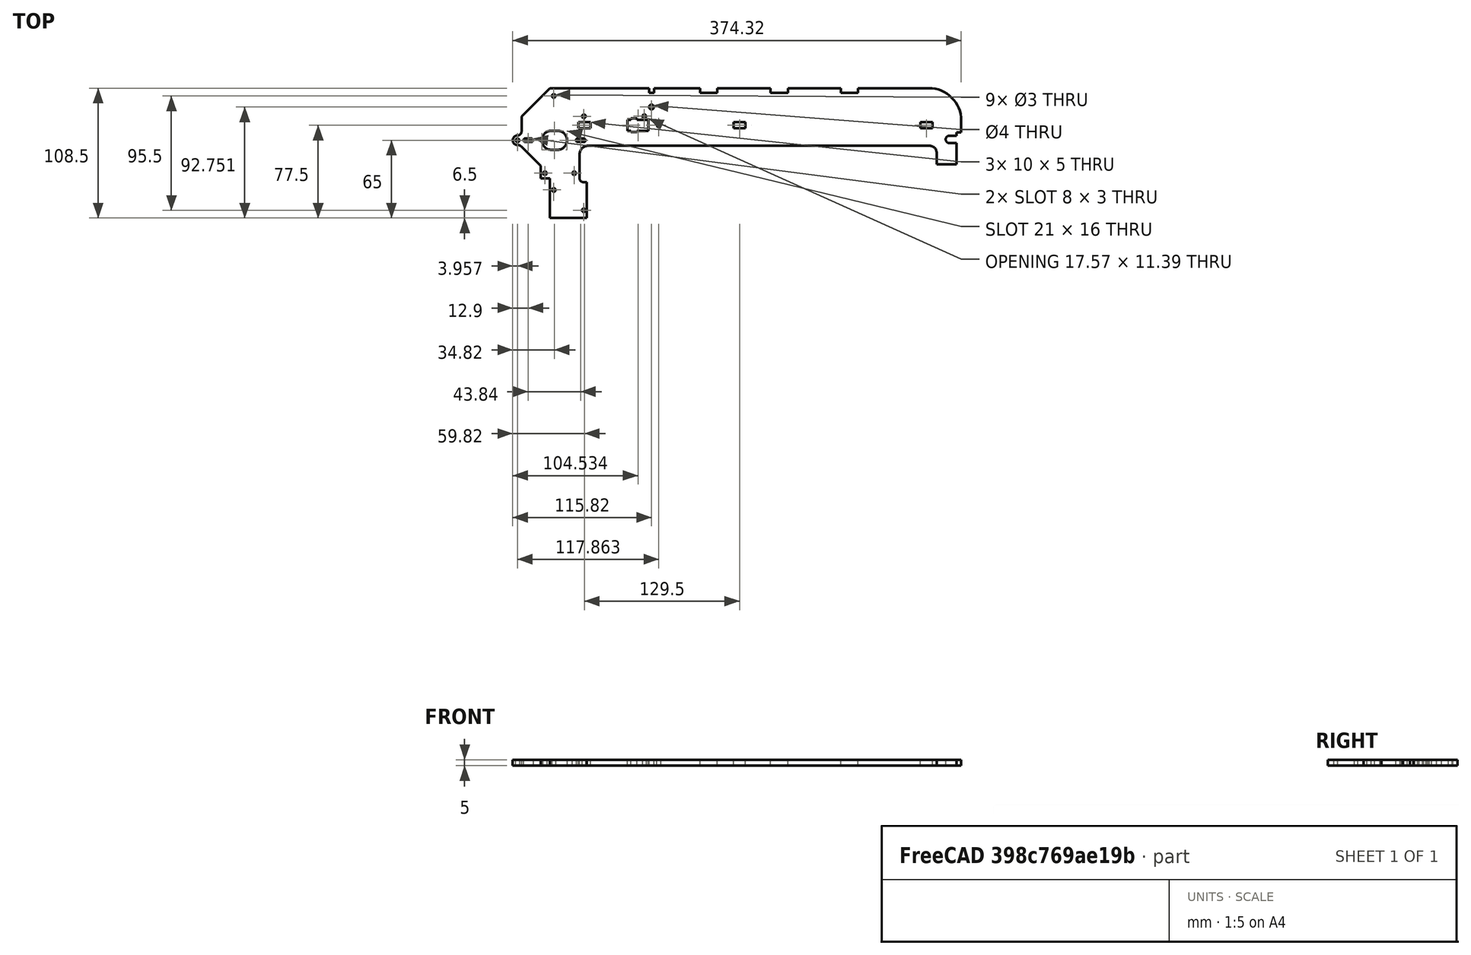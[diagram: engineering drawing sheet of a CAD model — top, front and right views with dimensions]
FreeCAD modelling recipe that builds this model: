
FCSTD DOCUMENT  (FreeCAD 0.17R13541 (Git))
Label: xx_561_x-axis-plate
License: All rights reserved
LicenseURL: http://en.wikipedia.org/wiki/All_rights_reserved
objects: Sketcher::SketchObject×1, PartDesign::Pad×1, PartDesign::Body×1
note: 4 computed .brp shape members not serialized (recipe doc carries the construction recipe); baked Part::Feature solids carry a one-line shape summary decoded from their .brp

FEATURE [Sketcher::SketchObject] Sketch090
  MapMode = 5
  Support = -> [XY_Plane]
  sketch-geometry (90):
    g0: Circle CenterX=78.5 CenterY=27.7514 CenterZ=0 NormalX=0 NormalY=0 NormalZ=-1 AngleXU=0 Radius=2
    g1: LineSegment StartX=66.4277 StartY=17 StartZ=0 EndX=66.4277 EndY=18.1939 EndZ=0
    g2: LineSegment StartX=24.5 StartY=-35 StartZ=0 EndX=21.5 EndY=-35 EndZ=0
    g3: LineSegment StartX=133.5 StartY=39.5 StartZ=0 EndX=119 EndY=39.5 EndZ=0
    g4: ArcOfCircle CenterX=21.92 CenterY=-1.78646e-06 CenterZ=0 NormalX=0 NormalY=0 NormalZ=1 AngleXU=0 Radius=1.5 StartAngle=4.7126 EndAngle=7.85377
    g5: LineSegment StartX=61.4277 StartY=6.8061 StartZ=0 EndX=66.4277 EndY=6.8061 EndZ=0
    g6: LineSegment StartX=-21.9203 StartY=1.5 StartZ=0 EndX=-26.9203 EndY=1.5 EndZ=0
    g7: ArcOfCircle CenterX=310 CenterY=16.5 CenterZ=0 NormalX=0 NormalY=0 NormalZ=1 AngleXU=0 Radius=27 StartAngle=0 EndAngle=1.5708
    g8: LineSegment StartX=333 StartY=-20 StartZ=0 EndX=333 EndY=-2.3 EndZ=0
    g9: LineSegment StartX=58.4277 StartY=17 StartZ=0 EndX=58.4277 EndY=8 EndZ=0
    g10: LineSegment StartX=-14 StartY=-21.3553 StartZ=0 EndX=-14 EndY=-32 EndZ=0
    g11: LineSegment StartX=25.5 StartY=-4.6 StartZ=0 EndX=310.5 EndY=-4.6 EndZ=0
    g12: Circle CenterX=-3.05 CenterY=-41.5 CenterZ=0 NormalX=0 NormalY=0 NormalZ=-1 AngleXU=0 Radius=1.5
    g13: Circle CenterX=84.5 CenterY=12.5 CenterZ=0 NormalX=0 NormalY=0 NormalZ=-1 AngleXU=0 Radius=1.5
    g14: LineSegment StartX=66.4277 StartY=18.1939 StartZ=0 EndX=61.4277 EndY=18.1939 EndZ=0
    g15: ArcOfCircle CenterX=-26.9203 CenterY=0 CenterZ=0 NormalX=0 NormalY=0 NormalZ=1 AngleXU=0 Radius=1.5 StartAngle=1.5708 EndAngle=4.71239
    g16: LineSegment StartX=80.5 StartY=43.5 StartZ=0 EndX=80.5 EndY=39.5 EndZ=0
    g17: LineSegment StartX=157 StartY=10 StartZ=0 EndX=157 EndY=15 EndZ=0
    g18: LineSegment StartX=61.4277 StartY=8 StartZ=0 EndX=61.4277 EndY=6.8061 EndZ=0
    g19: LineSegment StartX=313 StartY=10 StartZ=0 EndX=313 EndY=15 EndZ=0
    g20: Circle CenterX=22.05 CenterY=-58.5 CenterZ=0 NormalX=0 NormalY=0 NormalZ=-1 AngleXU=0 Radius=1.5
    g21: Circle CenterX=72.5 CenterY=20.1 CenterZ=0 NormalX=0 NormalY=0 NormalZ=-1 AngleXU=0 Radius=1.5
    g22: LineSegment StartX=-5 StartY=-8 StartZ=0 EndX=0 EndY=-8 EndZ=0
    g23: ArcOfCircle CenterX=-33.36 CenterY=0 CenterZ=0 NormalX=0 NormalY=0 NormalZ=1 AngleXU=0 Radius=3.96229 StartAngle=1.57159 EndAngle=4.7116
    g24: LineSegment StartX=76 StartY=8 StartZ=0 EndX=76 EndY=17 EndZ=0
    g25: LineSegment StartX=333 StartY=6.7 StartZ=0 EndX=337 EndY=6.7 EndZ=0
    g26: ArcOfCircle CenterX=-21.92 CenterY=0 CenterZ=0 NormalX=0 NormalY=0 NormalZ=1 AngleXU=0 Radius=1.5 StartAngle=4.71218 EndAngle=7.85419
    g27: LineSegment StartX=316.5 StartY=-10.6 StartZ=0 EndX=316.5 EndY=-20 EndZ=0
    g28: LineSegment StartX=303 StartY=10 StartZ=0 EndX=313 EndY=10 EndZ=0
    g29: LineSegment StartX=337 StartY=6.7 StartZ=0 EndX=337 EndY=16.5 EndZ=0
    g30: LineSegment StartX=313 StartY=15 StartZ=0 EndX=303 EndY=15 EndZ=0
    g31: LineSegment StartX=147 StartY=15 StartZ=0 EndX=147 EndY=10 EndZ=0
    g32: LineSegment StartX=-14 StartY=-32 StartZ=0 EndX=-6.5 EndY=-32 EndZ=0
    g33: LineSegment StartX=76.5 StartY=43.5 StartZ=0 EndX=-6.5 EndY=43.5 EndZ=0
    g34: LineSegment StartX=327 StartY=3.7 StartZ=0 EndX=333 EndY=3.7 EndZ=0
    g35: ArcOfCircle CenterX=-33.3631 CenterY=7.32541 CenterZ=0 NormalX=0 NormalY=0 NormalZ=1 AngleXU=0 Radius=3.36313 StartAngle=4.71239 EndAngle=6.28319
    g36: LineSegment StartX=-30 StartY=20 StartZ=0 EndX=-30 EndY=7.32541 EndZ=0
    g37: LineSegment StartX=177.75 StartY=43.5 StartZ=0 EndX=133.5 EndY=43.5 EndZ=0
    g38: LineSegment StartX=18.5 StartY=-32 StartZ=0 EndX=18.5 EndY=-11.6 EndZ=0
    g39: LineSegment StartX=-6.5 StartY=-32 StartZ=0 EndX=-6.5 EndY=-65 EndZ=0
    g40: LineSegment StartX=61.4277 StartY=18.1939 StartZ=0 EndX=61.4277 EndY=17 EndZ=0
    g41: Circle CenterX=-33.3631 CenterY=0 CenterZ=0 NormalX=0 NormalY=0 NormalZ=-1 AngleXU=0 Radius=1.5
    g42: LineSegment StartX=0 StartY=8 StartZ=0 EndX=-5 EndY=8 EndZ=0
    g43: LineSegment StartX=27.5 StartY=15 StartZ=0 EndX=17.5 EndY=15 EndZ=0
    g44: LineSegment StartX=316.5 StartY=-20 StartZ=0 EndX=333 EndY=-20 EndZ=0
    g45: LineSegment StartX=192.25 StartY=39.5 StartZ=0 EndX=177.75 EndY=39.5 EndZ=0
    g46: Circle CenterX=-10.5 CenterY=-27.55 CenterZ=0 NormalX=0 NormalY=0 NormalZ=-1 AngleXU=0 Radius=1.5
    g47: LineSegment StartX=119 StartY=43.5 StartZ=0 EndX=80.5 EndY=43.5 EndZ=0
    g48: ArcOfCircle CenterX=-5 CenterY=0 CenterZ=0 NormalX=0 NormalY=0 NormalZ=1 AngleXU=0 Radius=8 StartAngle=1.5708 EndAngle=4.71239
    g49: ArcOfCircle CenterX=310.5 CenterY=-10.6 CenterZ=0 NormalX=0 NormalY=0 NormalZ=1 AngleXU=0 Radius=6 StartAngle=0 EndAngle=1.5708
    g50: ArcOfCircle CenterX=25.5 CenterY=-11.6 CenterZ=0 NormalX=0 NormalY=0 NormalZ=1 AngleXU=0 Radius=7 StartAngle=1.5708 EndAngle=3.14159
    g51: LineSegment StartX=21.9203 StartY=1.5 StartZ=0 EndX=16.9203 EndY=1.5 EndZ=0
    g52: Circle CenterX=14 CenterY=-27.55 CenterZ=0 NormalX=0 NormalY=0 NormalZ=-1 AngleXU=0 Radius=1.5
    g53: LineSegment StartX=17.5 StartY=10 StartZ=0 EndX=27.5 EndY=10 EndZ=0
    g54: LineSegment StartX=177.75 StartY=39.5 StartZ=0 EndX=177.75 EndY=43.5 EndZ=0
    g55: LineSegment StartX=66.4277 StartY=8 StartZ=0 EndX=76 EndY=8 EndZ=0
    g56: Circle CenterX=-3.05 CenterY=37 CenterZ=0 NormalX=0 NormalY=0 NormalZ=-1 AngleXU=0 Radius=1.5
    g57: LineSegment StartX=76 StartY=17 StartZ=0 EndX=66.4277 EndY=17 EndZ=0
    g58: Circle CenterX=22.05 CenterY=20 CenterZ=0 NormalX=0 NormalY=0 NormalZ=-1 AngleXU=0 Radius=1.5
    g59: LineSegment StartX=-6.5 StartY=-65 StartZ=0 EndX=24.5 EndY=-65 EndZ=0
    g60: LineSegment StartX=310 StartY=43.5 StartZ=0 EndX=251 EndY=43.5 EndZ=0
    g61: ArcOfCircle CenterX=327 CenterY=0.7 CenterZ=0 NormalX=0 NormalY=0 NormalZ=1 AngleXU=0 Radius=3 StartAngle=1.5708 EndAngle=4.71239
    g62: LineSegment StartX=17.5 StartY=15 StartZ=0 EndX=17.5 EndY=10 EndZ=0
    g63: LineSegment StartX=303 StartY=15 StartZ=0 EndX=303 EndY=10 EndZ=0
    g64: LineSegment StartX=58.4277 StartY=8 StartZ=0 EndX=61.4277 EndY=8 EndZ=0
    g65: LineSegment StartX=333 StartY=3.7 StartZ=0 EndX=333 EndY=6.7 EndZ=0
    g66: LineSegment StartX=76.5 StartY=39.5 StartZ=0 EndX=76.5 EndY=43.5 EndZ=0
    g67: ArcOfCircle CenterX=21.5 CenterY=-32 CenterZ=0 NormalX=0 NormalY=0 NormalZ=1 AngleXU=0 Radius=3 StartAngle=3.14159 EndAngle=4.71239
    g68: LineSegment StartX=-26.9203 StartY=-1.5 StartZ=0 EndX=-21.9203 EndY=-1.5 EndZ=0
    g69: LineSegment StartX=24.5 StartY=-65 StartZ=0 EndX=24.5 EndY=-35 EndZ=0
    g70: LineSegment StartX=80.5 StartY=39.5 StartZ=0 EndX=76.5 EndY=39.5 EndZ=0
    g71: LineSegment StartX=192.25 StartY=43.5 StartZ=0 EndX=192.25 EndY=39.5 EndZ=0
    g72: LineSegment StartX=333 StartY=-2.3 StartZ=0 EndX=327 EndY=-2.3 EndZ=0
    g73: LineSegment StartX=133.5 StartY=43.5 StartZ=0 EndX=133.5 EndY=39.5 EndZ=0
    g74: LineSegment StartX=251 StartY=43.5 StartZ=0 EndX=251 EndY=39.5 EndZ=0
    g75: ArcOfCircle CenterX=-33.3631 CenterY=-8.71847 CenterZ=0 NormalX=0 NormalY=0 NormalZ=1 AngleXU=0 Radius=4.75618 StartAngle=0.785398 EndAngle=1.5708
    g76: LineSegment StartX=27.5 StartY=10 StartZ=0 EndX=27.5 EndY=15 EndZ=0
    g77: LineSegment StartX=66.4277 StartY=6.8061 StartZ=0 EndX=66.4277 EndY=8 EndZ=0
    g78: LineSegment StartX=-6.5 StartY=43.5 StartZ=0 EndX=-30 EndY=20 EndZ=0
    g79: LineSegment StartX=157 StartY=15 StartZ=0 EndX=147 EndY=15 EndZ=0
    g80: LineSegment StartX=-30 StartY=-5.35534 StartZ=0 EndX=-14 EndY=-21.3553 EndZ=0
    g81: LineSegment StartX=251 StartY=39.5 StartZ=0 EndX=236.5 EndY=39.5 EndZ=0
    g82: LineSegment StartX=236.5 StartY=43.5 StartZ=0 EndX=192.25 EndY=43.5 EndZ=0
    g83: LineSegment StartX=236.5 StartY=39.5 StartZ=0 EndX=236.5 EndY=43.5 EndZ=0
    g84: LineSegment StartX=16.9203 StartY=-1.5 StartZ=0 EndX=21.9203 EndY=-1.5 EndZ=0
    g85: LineSegment StartX=119 StartY=39.5 StartZ=0 EndX=119 EndY=43.5 EndZ=0
    g86: ArcOfCircle CenterX=16.9203 CenterY=0 CenterZ=0 NormalX=0 NormalY=0 NormalZ=1 AngleXU=0 Radius=1.5 StartAngle=1.5708 EndAngle=4.71239
    g87: LineSegment StartX=147 StartY=10 StartZ=0 EndX=157 EndY=10 EndZ=0
    g88: LineSegment StartX=61.4277 StartY=17 StartZ=0 EndX=58.4277 EndY=17 EndZ=0
    g89: ArcOfCircle CenterX=0 CenterY=0 CenterZ=0 NormalX=0 NormalY=0 NormalZ=1 AngleXU=0 Radius=8 StartAngle=4.71239 EndAngle=7.85398
  constraints (114):
    c: Coincident(g23,g75)
    c: Coincident(g23,g35)
    c: Coincident(g80,g75)
    c: Coincident(g36,g35)
    c: Coincident(g78,g36)
    c: Coincident(g15,g68)
    c: Coincident(g6,g15)
    c: Coincident(g68,g26)
    c: Coincident(g6,g26)
    c: Coincident(g10,g32)
    c: Coincident(g10,g80)
    c: Coincident(g59,g39)
    c: Coincident(g39,g32)
    c: Coincident(g33,g78)
    c: Coincident(g86,g84)
    c: Coincident(g51,g86)
    c: Coincident(g53,g62)
    c: Coincident(g62,g43)
    c: Coincident(g38,g67)
    c: Coincident(g50,g38)
    c: Coincident(g67,g2)
    c: Coincident(g84,g4)
    c: Coincident(g4,g51)
    c: Coincident(g69,g59)
    c: Coincident(g2,g69)
    c: Coincident(g11,g50)
    c: Coincident(g76,g53)
    c: Coincident(g76,g43)
    c: Coincident(g9,g64)
    c: Coincident(g88,g9)
    c: Coincident(g5,g18)
    c: Coincident(g18,g64)
    c: Coincident(g40,g88)
    c: Coincident(g14,g40)
    c: Coincident(g77,g5)
    c: Coincident(g55,g77)
    c: Coincident(g57,g1)
    c: Coincident(g1,g14)
    c: Coincident(g55,g24)
    c: Coincident(g57,g24)
    c: Coincident(g66,g70)
    c: Coincident(g33,g66)
    c: Coincident(g16,g70)
    c: Coincident(g16,g47)
    c: Coincident(g85,g3)
    c: Coincident(g85,g47)
    c: Coincident(g73,g3)
    c: Coincident(g37,g73)
    c: Coincident(g31,g87)
    c: Coincident(g31,g79)
    c: Coincident(g17,g87)
    c: Coincident(g79,g17)
    c: Coincident(g54,g45)
    c: Coincident(g54,g37)
    c: Coincident(g45,g71)
    c: Coincident(g71,g82)
    c: Coincident(g83,g81)
    c: Coincident(g83,g82)
    c: Coincident(g81,g74)
    c: Coincident(g74,g60)
    c: Coincident(g28,g63)
    c: Coincident(g63,g30)
    c: Coincident(g7,g60)
    c: Coincident(g49,g11)
    c: Coincident(g19,g28)
    c: Coincident(g19,g30)
    c: Coincident(g27,g44)
    c: Coincident(g27,g49)
    c: Coincident(g61,g72)
    c: Coincident(g34,g61)
    c: Coincident(g44,g8)
    c: Coincident(g72,g8)
    c: Coincident(g34,g65)
    c: Coincident(g25,g65)
    c: Coincident(g25,g29)
    c: Coincident(g29,g7)
    c: PointOnObject(g23,g-1)
    c: PointOnObject(g15,g-1)
    c: PointOnObject(g26,g-1)
    c: PointOnObject(g48,g-1)
    c: Coincident(g89,g-1)
    c: Radius(g48) = 8
    c: Equal(g48,g89)
    c: Tangent(g42,g48) = -1.5708
    c: Tangent(g42,g89) = -1.5708
    c: Tangent(g22,g89) = -1.5708
    c: Tangent(g22,g48) = -1.5708
    c: Radius(g41) = 1.5
    c: Equal(g41,g15)
    c: Equal(g15,g26)
    c: Equal(g26,g86)
    c: Equal(g86,g4)
    c: Equal(g4,g58)
    c: Equal(g58,g21)
    c: Equal(g21,g13)
    c: Equal(g13,g56)
    c: Equal(g56,g46)
    c: Equal(g46,g52)
    c: Equal(g52,g12)
    c: Equal(g12,g20)
    c: DistanceX(g-2,g56) = -3.05
    c: DistanceY(g-1,g56) = 37
    c: DistanceX(g-2,g58) = 22.05
    c: DistanceY(g-1,g58) = 20
    c: Distance(g26,g4) = 43.84
    c: Equal(g84,g68)
    c: Equal(g68,g22)
    c: Distance(g22) = 5
    c: DistanceX(g-2,g4) = 21.92
    c: DistanceX(g-2,g23) = -33.36
    c: DistanceX(g-2,g21) = 72.5
    c: DistanceX(g-2,g13) = 84.5
    c: DistanceY(g-1,g21) = 20.1
    c: DistanceY(g-1,g13) = 12.5
FEATURE [PartDesign::Pad] Pad
  Length = 5
  Length2 = 100
  Profile = -> Sketch090
  Type = 0
FEATURE [PartDesign::Body] Body
  Group = -> [Sketch090,Pad]
  Origin = -> Origin
  Tip = -> Pad
